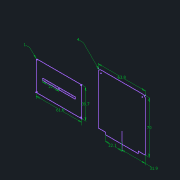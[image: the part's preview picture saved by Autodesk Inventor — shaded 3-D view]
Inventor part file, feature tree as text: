
AUTODESK INVENTOR PART (.ipt)
format: ipt  version: 2021 (Build 250183000, 183)  size: 81,920 bytes
history: native  units: mm
features: sketch x1
ambient origin geometry x8: Origin, YZ Plane, XZ Plane, XY Plane, X Axis, Y Axis, Z Axis, Center Point
feature tree (1):
  sketch  "Sketch1"  dims[d0=61.6mm d1=39.7mm d2=1.0mm d5=22.0mm d7=63.8mm d8=70.0mm d9=3.0mm d10=31.9mm d11=22.1mm d12=4.0mm]
